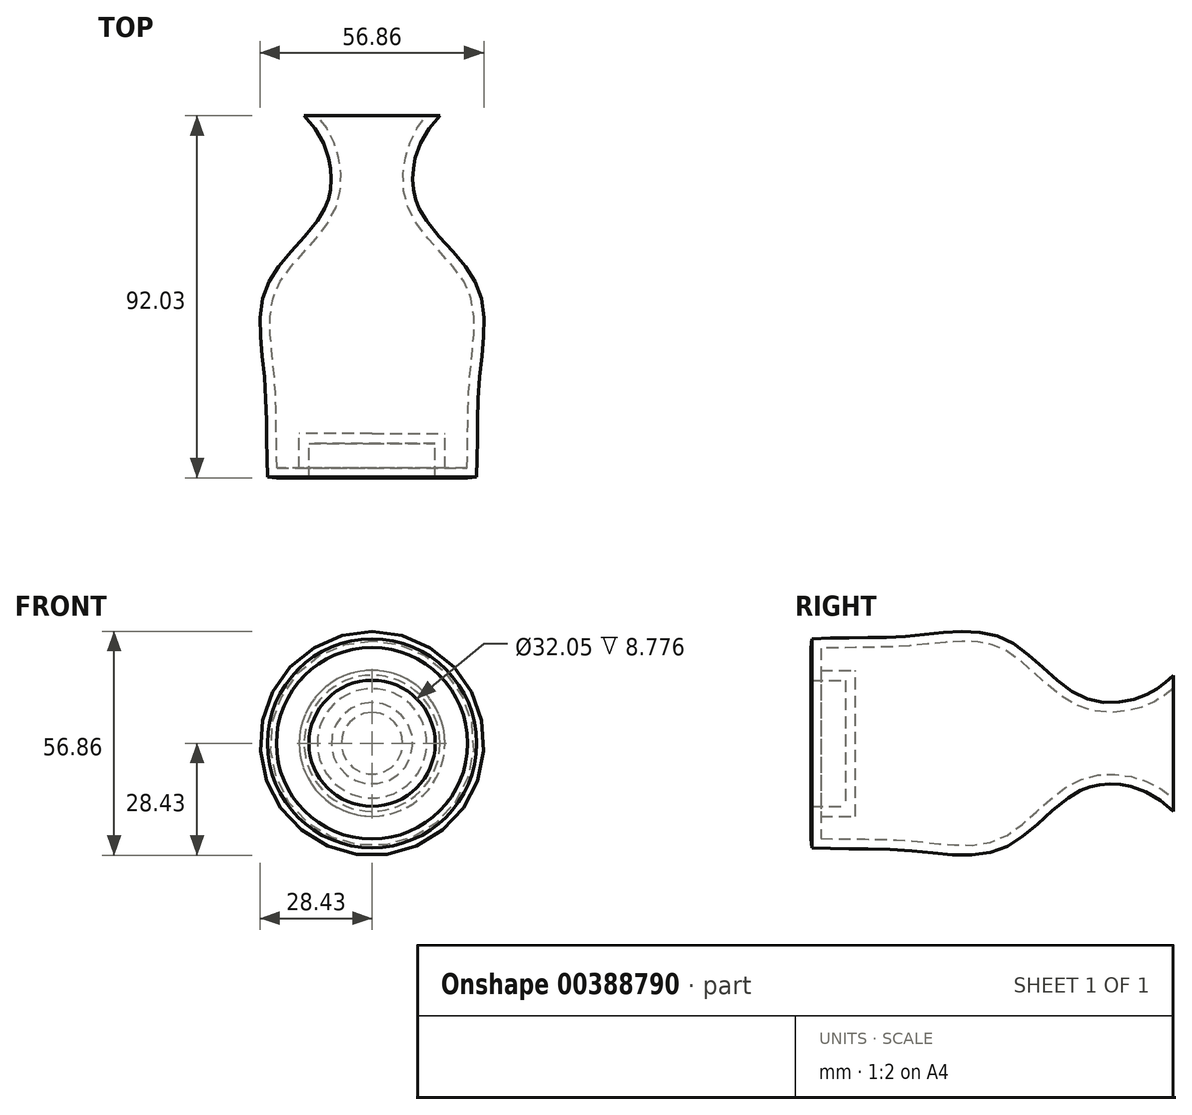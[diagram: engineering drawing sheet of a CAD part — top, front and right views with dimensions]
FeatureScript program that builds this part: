
annotation { "Feature Type Name" : "Feature", "Feature Type Description" : "" }
export const myFeature = defineFeature(function(context is Context, id is Id, definition is map)
    precondition{}
    {
        {
            var Q0;
            Q0=qCreatedBy(makeId("Top.planeOp"),FACE);
            var sketch = newSketch(context, id + "F0", { "sketchPlane" : qUnion([Q0])});
            skLineSegment(sketch, "E0", {"start": v(0, 39.44) * mm, "end": v(0, -43.81) * mm});
            skLineSegment(sketch, "E1", {"start": v(16.03, -43.81) * mm, "end": v(16.03, -52.59) * mm});
            skLineSegment(sketch, "E2", {"start": v(16.03, -52.59) * mm, "end": v(24.3, -52.59) * mm});
            skLineSegment(sketch, "E3", {"start": v(16.03, -43.81) * mm, "end": v(0, -43.81) * mm});
            skLineSegment(sketch, "E4", {"start": v(17.28, 39.44) * mm, "end": v(0, 39.44) * mm});
            skFitSpline(sketch, "E5", {"points": [v(17.28, 39.44) * mm, v(12.27, 32.41) * mm, v(11.76, 16.37) * mm, v(26.56, -3.44) * mm, v(27.31, -27.26) * mm, v(26.56, -52.34) * mm], "startDerivative": vector(-41.35, -43.97) * mm, "endDerivative": vector(-5.7, -109.08) * mm});
            skLineSegment(sketch, "E6", {"start": v(24.3, -52.59) * mm, "end": v(26.56, -52.34) * mm});
            skSolve(sketch);
        }
        {
            var Q0;
            Q0 = qSketchRegion(id + "F0", true);
            var Q1;
            Q1=sQuery(id+"F0.wireOp",EDGE,"E0");
            revolve(context, id + "F1", {"entities" : qUnion([Q0]), "axis" : qUnion([Q1]), "revolveType" : RevolveType.FULL});
        }
        {
            var Q0;
            Q0=makeQuery(id+"F1.opRevolve","SWEPT_FACE",FACE,{"disambiguationData":[OSD([sQuery(id+"F0.wireOp",EDGE,"E4")])]});
            shell(context, id + "F2", {"entities" : qUnion([Q0]), "thickness" : 2.5 * mm});
        }
    });
